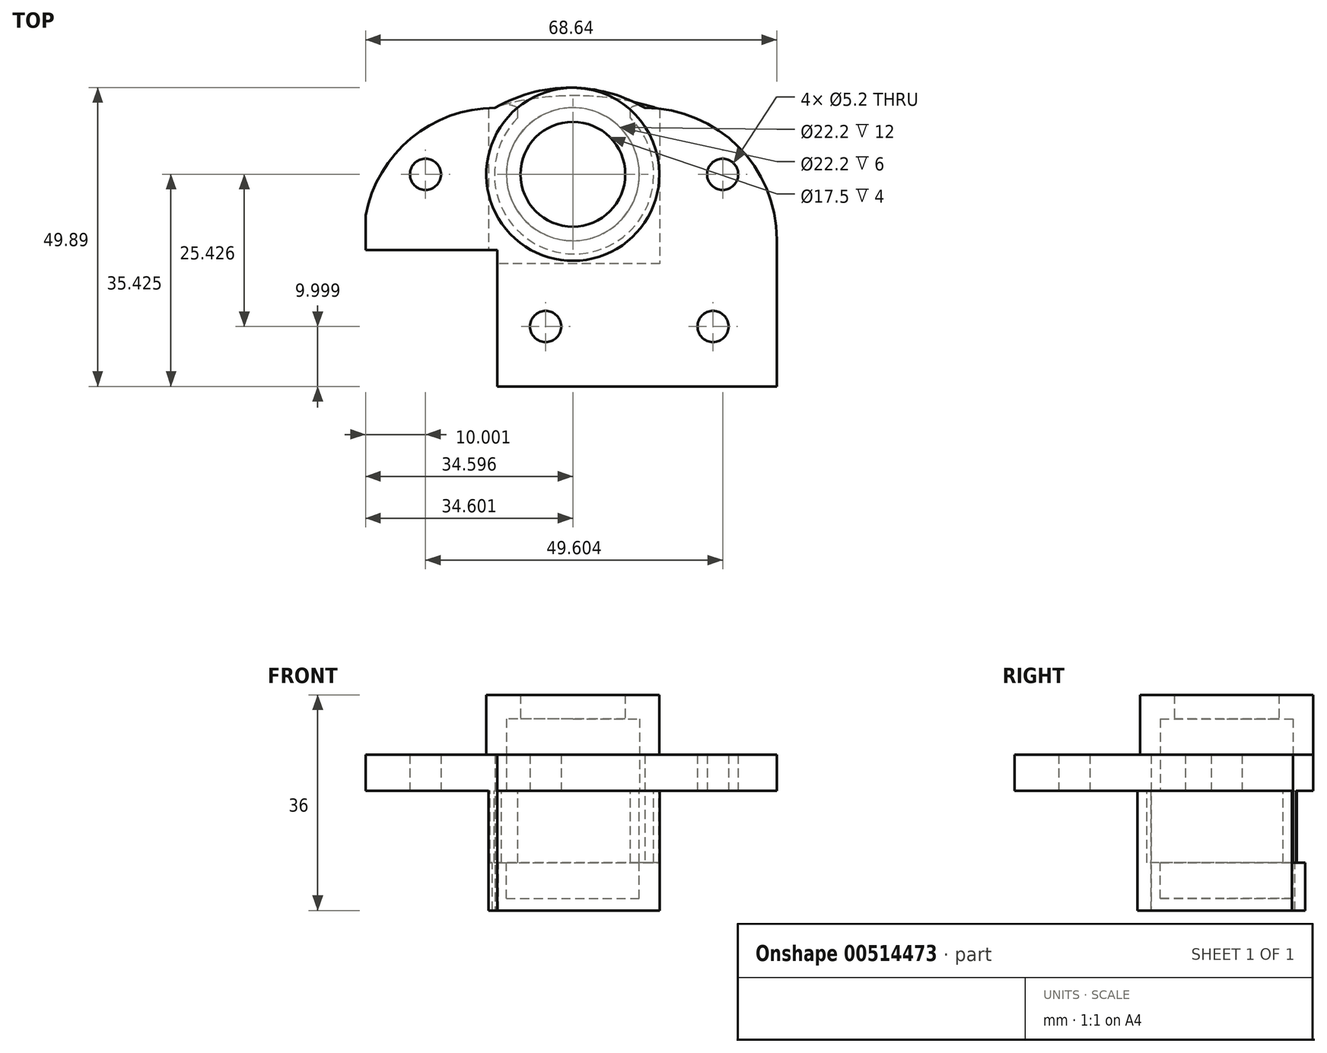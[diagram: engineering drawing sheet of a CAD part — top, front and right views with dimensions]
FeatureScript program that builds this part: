
annotation { "Feature Type Name" : "Feature", "Feature Type Description" : "" }
export const myFeature = defineFeature(function(context is Context, id is Id, definition is map)
    precondition{}
    {
        {
            var Q0;
            Q0=qCreatedBy(makeId("Top.planeOp"),FACE);
            var sketch = newSketch(context, id + "F0", { "sketchPlane" : qUnion([Q0])});
            skLineSegment(sketch, "E0", {"start": v(-15.33, -19.87) * mm, "end": v(6.68, -19.87) * mm});
            skLineSegment(sketch, "E1", {"start": v(6.68, -19.87) * mm, "end": v(6.68, -42.67) * mm});
            skLineSegment(sketch, "E2", {"start": v(6.68, -42.67) * mm, "end": v(53.3, -42.67) * mm});
            skLineSegment(sketch, "E3", {"start": v(53.3, -42.67) * mm, "end": v(53.3, -18.17) * mm});
            skCircle(sketch, "E4", {"center": v(-5.33, -7.24) * mm, "radius": 2.6 * mm});
            skCircle(sketch, "E5", {"center": v(14.72, -32.67) * mm, "radius": 2.6 * mm});
            skCircle(sketch, "E6", {"center": v(44.28, -7.24) * mm, "radius": 2.6 * mm});
            skCircle(sketch, "E7", {"center": v(42.67, -32.67) * mm, "radius": 2.6 * mm});
            skCircle(sketch, "E8", {"center": v(19.27, -7.24) * mm, "radius": 11.1 * mm});
            skPoint(sketch, "E9.visualSharp", {"position": v(-15.7, 3.83) * mm});
            skArc(sketch, "E9.filletArc", {"start": v(6.3, 3.83) * mm, "mid": v(-7.76, -1.25) * mm, "end": v(-15.33, -14.14) * mm});
            skPoint(sketch, "E10.visualSharp", {"position": v(53.3, 3.83) * mm});
            skArc(sketch, "E10.filletArc", {"start": v(53.3, -18.17) * mm, "mid": v(46.86, -2.61) * mm, "end": v(31.3, 3.83) * mm});
            skLineSegment(sketch, "E11.bottom", {"start": v(4.67, -23.98) * mm, "end": v(-15.33, -23.98) * mm, "construction": true});
            skLineSegment(sketch, "E11.top", {"start": v(4.67, 9.5) * mm, "end": v(-15.33, 9.5) * mm, "construction": true});
            skLineSegment(sketch, "E11.left", {"start": v(4.67, -23.98) * mm, "end": v(4.67, 9.5) * mm, "construction": true});
            skLineSegment(sketch, "E11.right", {"start": v(-15.33, -23.98) * mm, "end": v(-15.33, 9.5) * mm, "construction": true});
            skLineSegment(sketch, "E12.bottom", {"start": v(34.28, -26.24) * mm, "end": v(54.28, -26.24) * mm, "construction": true});
            skLineSegment(sketch, "E12.top", {"start": v(34.28, 11.76) * mm, "end": v(54.28, 11.76) * mm, "construction": true});
            skLineSegment(sketch, "E12.left", {"start": v(34.28, -26.24) * mm, "end": v(34.28, 11.76) * mm, "construction": true});
            skLineSegment(sketch, "E12.right", {"start": v(54.28, -26.24) * mm, "end": v(54.28, 11.76) * mm, "construction": true});
            skLineSegment(sketch, "E13", {"start": v(-5.33, -7.24) * mm, "end": v(44.28, -7.24) * mm, "construction": true});
            skLineSegment(sketch, "E14", {"start": v(-15.33, -14.14) * mm, "end": v(-15.33, -19.87) * mm});
            skArc(sketch, "E15", {"start": v(31.3, 3.83) * mm, "mid": v(18.8, 7.22) * mm, "end": v(6.3, 3.83) * mm});
            skSolve(sketch);
        }
        {
            var Q0;
            Q0=makeQuery(id+"F0.imprint","IMPRINT",FACE,{"disambiguationData":[TD([[makeQuery(id+"F0.imprint","IMPRINT",EDGE,{"derivedFrom":sQuery(id+"F0.wireOp",EDGE,"E0")}),1.0]])]});
            extrude(context, id + "F1", {"entities" : qUnion([Q0]), "depth" : 6 * mm});
        }
        {
            var Q0;
            Q0=makeQuery(id+"F1.opExtrude","CAP_FACE",FACE,{"disambiguationData":[OSD([sQuery(id+"F0.wireOp",EDGE,"E0"),sQuery(id+"F0.wireOp",EDGE,"E1"),sQuery(id+"F0.wireOp",EDGE,"E2"),sQuery(id+"F0.wireOp",EDGE,"E3"),sQuery(id+"F0.wireOp",EDGE,"5161356e-f96a-417a-a71d-a5da409e1e9f"),sQuery(id+"F0.wireOp",EDGE,"E4"),sQuery(id+"F0.wireOp",EDGE,"E5"),sQuery(id+"F0.wireOp",EDGE,"E6"),sQuery(id+"F0.wireOp",EDGE,"E7"),sQuery(id+"F0.wireOp",EDGE,"E8"),sQuery(id+"F0.wireOp",EDGE,"E9.filletArc"),sQuery(id+"F0.wireOp",EDGE,"E10.filletArc"),sQuery(id+"F0.wireOp",EDGE,"E14")])],"isStart":true});
            var sketch = newSketch(context, id + "F2", { "sketchPlane" : qUnion([Q0])});
            skCircle(sketch, "E16", {"center": v(22.27, 8.67) * mm, "radius": 4 * mm, "construction": true});
            skLineSegment(sketch, "E17.bottom", {"start": v(44.28, 7.24) * mm, "end": v(34.28, 7.24) * mm, "construction": true});
            skLineSegment(sketch, "E17.top", {"start": v(44.28, 22.67) * mm, "end": v(39.28, 22.67) * mm, "construction": true});
            skLineSegment(sketch, "E17.left", {"start": v(44.28, 7.24) * mm, "end": v(44.28, 22.67) * mm, "construction": true});
            skLineSegment(sketch, "E17.right", {"start": v(34.28, 7.24) * mm, "end": v(34.28, 22.67) * mm, "construction": true});
            skLineSegment(sketch, "E18.bottom", {"start": v(-5.33, 7.24) * mm, "end": v(4.67, 7.24) * mm, "construction": true});
            skLineSegment(sketch, "E18.left", {"start": v(-5.33, 7.24) * mm, "end": v(-5.33, 22.67) * mm, "construction": true});
            skLineSegment(sketch, "E18.right", {"start": v(4.67, 7.24) * mm, "end": v(4.67, 22.67) * mm, "construction": true});
            skLineSegment(sketch, "E19", {"start": v(19.47, 8.67) * mm, "end": v(19.47, -3.83) * mm, "construction": true});
            skPoint(sketch, "E20.oppositeSnap0", {"position": v(39.28, 22.67) * mm});
            skLineSegment(sketch, "E20.bottom", {"start": v(42.67, 32.67) * mm, "end": v(-12.73, 32.67) * mm, "construction": true});
            skLineSegment(sketch, "E20.top", {"start": v(42.67, 22.67) * mm, "end": v(39.28, 22.67) * mm, "construction": true});
            skLineSegment(sketch, "E20.left", {"start": v(42.67, 32.67) * mm, "end": v(42.67, 22.67) * mm, "construction": true});
            skLineSegment(sketch, "E20.right", {"start": v(-12.73, 32.67) * mm, "end": v(-12.73, 22.67) * mm, "construction": true});
            skLineSegment(sketch, "E21", {"start": v(4.67, 7.24) * mm, "end": v(34.28, 7.24) * mm, "construction": true});
            skArc(sketch, "E22.0", {"start": v(28.87, -2.17) * mm, "mid": v(19.47, 20.54) * mm, "end": v(10.08, -2.17) * mm});
            skLineSegment(sketch, "E23", {"start": v(28.87, -2.17) * mm, "end": v(28.87, -3.83) * mm});
            skLineSegment(sketch, "E24", {"start": v(10.08, -2.17) * mm, "end": v(10.08, -3.83) * mm});
            skLineSegment(sketch, "E25", {"start": v(4.67, 7.24) * mm, "end": v(4.67, -3.77) * mm});
            skLineSegment(sketch, "E26", {"start": v(34.28, 7.24) * mm, "end": v(34.28, -3.63) * mm, "construction": true});
            skLineSegment(sketch, "E27.trimOffspring", {"start": v(34.28, 22.67) * mm, "end": v(4.67, 22.67) * mm, "construction": true});
            skLineSegment(sketch, "E28.trimOffspring", {"start": v(-5.33, 22.67) * mm, "end": v(-12.73, 22.67) * mm, "construction": true});
            skLineSegment(sketch, "E29.0", {"start": v(5.17, 7.24) * mm, "end": v(5.17, -3.63) * mm});
            skLineSegment(sketch, "E29.1", {"start": v(33.78, 7.24) * mm, "end": v(33.78, -3.63) * mm});
            skLineSegment(sketch, "E29.2", {"start": v(33.78, 7.24) * mm, "end": v(33.78, 22.17) * mm});
            skLineSegment(sketch, "E29.3", {"start": v(33.78, 22.17) * mm, "end": v(6.68, 22.17) * mm});
            skLineSegment(sketch, "E29.4", {"start": v(5.17, 7.24) * mm, "end": v(5.17, 19.87) * mm});
            skArc(sketch, "E30", {"start": v(28.87, -3.83) * mm, "mid": v(31.35, -4.44) * mm, "end": v(33.78, -3.63) * mm});
            skArc(sketch, "E31.MirrorCS", {"start": v(10.08, -3.83) * mm, "mid": v(7.6, -4.44) * mm, "end": v(5.17, -3.63) * mm});
            skLineSegment(sketch, "E32.trimOffspring", {"start": v(5.17, -3.77) * mm, "end": v(5.17, -3.77) * mm});
            skLineSegment(sketch, "E33", {"start": v(6.68, 22.17) * mm, "end": v(6.68, 19.87) * mm});
            skLineSegment(sketch, "E34", {"start": v(6.68, 19.87) * mm, "end": v(5.17, 19.87) * mm});
            skLineSegment(sketch, "E35", {"start": v(-5.33, 7.24) * mm, "end": v(44.28, 7.24) * mm, "construction": true});
            skSolve(sketch);
        }
        {
            var Q0;
            Q0=makeQuery(id+"F2.imprint","IMPRINT",FACE,{"disambiguationData":[TD([[makeQuery(id+"F2.imprint","IMPRINT",EDGE,{"derivedFrom":sQuery(id+"F2.wireOp",EDGE,"E22.0")}),-1.0]])]});
            extrude(context, id + "F3", {"entities" : qUnion([Q0]), "operationType" : NewBodyOperationType.ADD, "depth" : 12 * mm});
        }
        {
            var Q0;
            Q0=makeQuery(id+"F3.opExtrude","CAP_FACE",FACE,{"disambiguationData":[OSD([sQuery(id+"F0.wireOp",EDGE,"E9.filletArc"),sQuery(id+"F0.wireOp",EDGE,"E10.filletArc"),sQuery(id+"F0.wireOp",EDGE,"qHf0stzJ-jH66-dw9K-h3hp-NyYAEVTUKJMS"),sQuery(id+"F2.wireOp",EDGE,"E22.0"),sQuery(id+"F2.wireOp",EDGE,"E23"),sQuery(id+"F2.wireOp",EDGE,"E24"),sQuery(id+"F2.wireOp",EDGE,"E29.0"),sQuery(id+"F2.wireOp",EDGE,"E29.1"),sQuery(id+"F2.wireOp",EDGE,"E29.2"),sQuery(id+"F2.wireOp",EDGE,"E29.3"),sQuery(id+"F2.wireOp",EDGE,"E29.4"),sQuery(id+"F2.wireOp",EDGE,"E30"),sQuery(id+"F2.wireOp",EDGE,"E31.MirrorCS"),sQuery(id+"F2.wireOp",EDGE,"E33"),sQuery(id+"F2.wireOp",EDGE,"E34")])],"isStart":false});
            var sketch = newSketch(context, id + "F4", { "sketchPlane" : qUnion([Q0])});
            skLineSegment(sketch, "E36", {"start": v(5.17, -3.63) * mm, "end": v(5.17, 19.87) * mm});
            skLineSegment(sketch, "E37", {"start": v(5.17, 19.87) * mm, "end": v(6.68, 19.87) * mm});
            skLineSegment(sketch, "E38", {"start": v(6.68, 19.87) * mm, "end": v(6.68, 22.17) * mm});
            skLineSegment(sketch, "E39", {"start": v(6.68, 22.17) * mm, "end": v(33.78, 22.17) * mm});
            skLineSegment(sketch, "E40", {"start": v(33.78, 22.17) * mm, "end": v(33.78, -3.63) * mm});
            skArc(sketch, "E41", {"start": v(5.17, -3.63) * mm, "mid": v(19.47, -5.87) * mm, "end": v(33.78, -3.63) * mm});
            skCircle(sketch, "E42", {"center": v(19.27, 7.24) * mm, "radius": 11.1 * mm});
            skSolve(sketch);
        }
        {
            var Q0;
            {var subQ9=sQuery(id+"F4.wireOp",EDGE,"E36");Q0=makeQuery(id+"F4.imprint","IMPRINT",FACE,{"disambiguationData":[TD([[makeQuery(id+"F4.imprint","IMPRINT",EDGE,{"derivedFrom":subQ9}),-1.0]])]});}
            var Q1;
            Q1=makeQuery(id+"F4.imprint","IMPRINT",FACE,{"disambiguationData":[TD([[makeQuery(id+"F4.imprint","IMPRINT",EDGE,{"derivedFrom":makeQuery(id+"F3.opExtrude","CAP_EDGE",EDGE,{"disambiguationData":[OSD([sQuery(id+"F2.wireOp",EDGE,"E22.0")])],"isStart":false})}),1.0]])]});
            extrude(context, id + "F5", {"entities" : qUnion([Q0, Q1]), "operationType" : NewBodyOperationType.ADD, "depth" : 6 * mm});
        }
        {
            var Q0;
            Q0=makeQuery(id+"F5.opExtrude","CAP_FACE",FACE,{"disambiguationData":[OSD([sQuery(id+"F4.wireOp",EDGE,"E36"),sQuery(id+"F4.wireOp",EDGE,"E37"),sQuery(id+"F4.wireOp",EDGE,"E38"),sQuery(id+"F4.wireOp",EDGE,"E39"),sQuery(id+"F4.wireOp",EDGE,"E40"),sQuery(id+"F4.wireOp",EDGE,"E41"),sQuery(id+"F4.wireOp",EDGE,"E42")])],"isStart":false});
            var sketch = newSketch(context, id + "F6", { "sketchPlane" : qUnion([Q0])});
            skLineSegment(sketch, "E43.0", {"start": v(33.78, 22.17) * mm, "end": v(6.68, 22.17) * mm});
            skLineSegment(sketch, "E43.1", {"start": v(33.78, 22.17) * mm, "end": v(33.78, -3.63) * mm});
            skArc(sketch, "E43.2", {"start": v(5.17, -3.63) * mm, "mid": v(19.47, -5.87) * mm, "end": v(33.78, -3.63) * mm});
            skLineSegment(sketch, "E43.3", {"start": v(5.17, -3.63) * mm, "end": v(5.17, 19.87) * mm});
            skLineSegment(sketch, "E43.4", {"start": v(5.17, 19.87) * mm, "end": v(6.68, 19.87) * mm});
            skLineSegment(sketch, "E43.5", {"start": v(6.68, 19.87) * mm, "end": v(6.68, 22.17) * mm});
            skSolve(sketch);
        }
        {
            var Q0;
            Q0=makeQuery(id+"F6.imprint","IMPRINT",FACE,{"disambiguationData":[TD([[makeQuery(id+"F6.imprint","IMPRINT",EDGE,{"derivedFrom":sQuery(id+"F6.wireOp",EDGE,"E43.0")}),1.0]])]});
            var Q1;
            Q1=makeQuery(id+"F6.imprint","IMPRINT",FACE,{"disambiguationData":[TD([[makeQuery(id+"F6.imprint","IMPRINT",EDGE,{"derivedFrom":makeQuery(id+"F5.opExtrude","CAP_EDGE",EDGE,{"disambiguationData":[OSD([sQuery(id+"F4.wireOp",EDGE,"E42")])],"isStart":false})}),1.0]])]});
            extrude(context, id + "F7", {"entities" : qUnion([Q0, Q1]), "operationType" : NewBodyOperationType.ADD, "depth" : 2 * mm});
        }
        {
            var Q0;
            Q0=makeQuery(id+"F1.opExtrude","CAP_FACE",FACE,{"disambiguationData":[OSD([sQuery(id+"F0.wireOp",EDGE,"E0"),sQuery(id+"F0.wireOp",EDGE,"E1"),sQuery(id+"F0.wireOp",EDGE,"E2"),sQuery(id+"F0.wireOp",EDGE,"E3"),sQuery(id+"F0.wireOp",EDGE,"E4"),sQuery(id+"F0.wireOp",EDGE,"E5"),sQuery(id+"F0.wireOp",EDGE,"E6"),sQuery(id+"F0.wireOp",EDGE,"E7"),sQuery(id+"F0.wireOp",EDGE,"E8"),sQuery(id+"F0.wireOp",EDGE,"E9.filletArc"),sQuery(id+"F0.wireOp",EDGE,"E10.filletArc"),sQuery(id+"F0.wireOp",EDGE,"E14"),sQuery(id+"F0.wireOp",EDGE,"E15")])],"isStart":false});
            var sketch = newSketch(context, id + "F8", { "sketchPlane" : qUnion([Q0])});
            skCircle(sketch, "E44.0", {"center": v(19.27, -7.24) * mm, "radius": 11.1 * mm});
            skCircle(sketch, "E45", {"center": v(19.27, -7.24) * mm, "radius": 14.44 * mm});
            skSolve(sketch);
        }
        {
            var Q0;
            Q0=makeQuery(id+"F8.imprint","IMPRINT",FACE,{"disambiguationData":[TD([[makeQuery(id+"F8.imprint","IMPRINT",EDGE,{"derivedFrom":sQuery(id+"F8.wireOp",EDGE,"E45")}),1.0]])]});
            extrude(context, id + "F9", {"entities" : qUnion([Q0]), "operationType" : NewBodyOperationType.ADD, "depth" : 6 * mm});
        }
        {
            var Q0;
            Q0=makeQuery(id+"F9.opExtrude","CAP_FACE",FACE,{"disambiguationData":[OSD([sQuery(id+"F0.wireOp",EDGE,"E8"),sQuery(id+"F8.wireOp",EDGE,"E45")])],"isStart":false});
            var sketch = newSketch(context, id + "F10", { "sketchPlane" : qUnion([Q0])});
            skCircle(sketch, "E46.0", {"center": v(19.27, -7.24) * mm, "radius": 14.44 * mm});
            skCircle(sketch, "E47", {"center": v(19.27, -7.24) * mm, "radius": 8.75 * mm});
            skSolve(sketch);
        }
        {
            var Q0;
            Q0=makeQuery(id+"F10.imprint","IMPRINT",FACE,{"disambiguationData":[TD([[makeQuery(id+"F10.imprint","IMPRINT",EDGE,{"derivedFrom":sQuery(id+"F10.wireOp",EDGE,"E46.0")}),1.0]])]});
            var Q1;
            Q1=makeQuery(id+"F10.imprint","IMPRINT",FACE,{"disambiguationData":[TD([[makeQuery(id+"F10.imprint","IMPRINT",EDGE,{"derivedFrom":sQuery(id+"F10.wireOp",EDGE,"E47")}),-1.0]])]});
            extrude(context, id + "F11", {"entities" : qUnion([Q0, Q1]), "operationType" : NewBodyOperationType.ADD, "depth" : 4 * mm});
        }
    });
